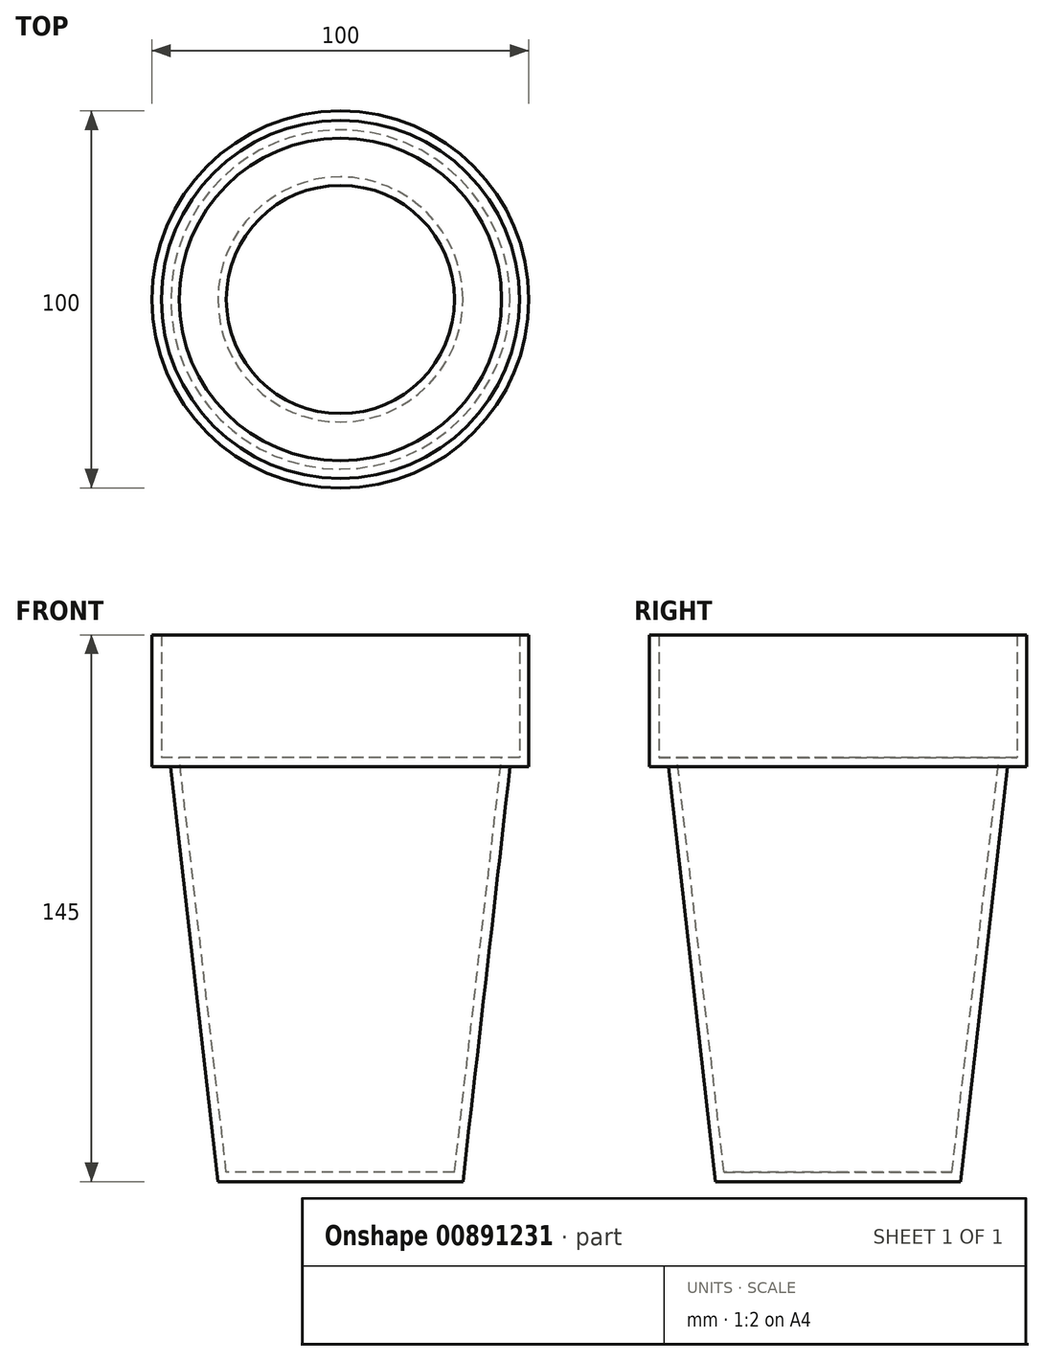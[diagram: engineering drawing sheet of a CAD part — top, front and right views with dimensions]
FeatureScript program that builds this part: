
annotation { "Feature Type Name" : "Feature", "Feature Type Description" : "" }
export const myFeature = defineFeature(function(context is Context, id is Id, definition is map)
    precondition{}
    {
        {
            var Q0;
            Q0=qCreatedBy(makeId("Top.planeOp"),FACE);
            var sketch = newSketch(context, id + "F0", { "sketchPlane" : qUnion([Q0])});
            skCircle(sketch, "E0", {"center": v(0, 0) * mm, "radius": 32.5 * mm});
            skSolve(sketch);
        }
        {
            var Q0;
            Q0=qCreatedBy(makeId("Top.planeOp"),FACE);
            cPlane(context, id + "F1", {"entities" : qUnion([Q0]), "cplaneType" : CPlaneType.OFFSET, "offset" : 110 * mm, "width" : 150 * mm, "height" : 150 * mm});
        }
        {
            var Q0;
            Q0=qCreatedBy(id+"F1.planeOp",FACE);
            var sketch = newSketch(context, id + "F2", { "sketchPlane" : qUnion([Q0])});
            skCircle(sketch, "E1", {"center": v(0, 0) * mm, "radius": 45 * mm});
            skSolve(sketch);
        }
        {
            var Q0;
            Q0=makeQuery(id+"F0.imprint","IMPRINT",FACE,{"disambiguationData":[TD([[makeQuery(id+"F0.imprint","IMPRINT",EDGE,{"derivedFrom":sQuery(id+"F0.wireOp",EDGE,"E0")}),1.0]])]});
            var Q1;
            Q1=makeQuery(id+"F2.imprint","IMPRINT",FACE,{"disambiguationData":[TD([[makeQuery(id+"F2.imprint","IMPRINT",EDGE,{"derivedFrom":sQuery(id+"F2.wireOp",EDGE,"E1")}),1.0]])]});
            loft(context, id + "F3", {"sheetProfilesArray" : [{ "sheetProfileEntities" : qUnion([Q0]) }, { "sheetProfileEntities" : qUnion([Q1]) }]});
        }
        {
            var Q0;
            Q0=makeQuery(id+"F3.opLoft","CAP_FACE",FACE,{"disambiguationData":[OSD([makeQuery(id+"F2.imprint","IMPRINT",FACE,{"disambiguationData":[TD([[makeQuery(id+"F2.imprint","IMPRINT",EDGE,{"derivedFrom":sQuery(id+"F2.wireOp",EDGE,"E1")}),1.0]])]})])],"isStart":true});
            var sketch = newSketch(context, id + "F4", { "sketchPlane" : qUnion([Q0])});
            skCircle(sketch, "E2", {"center": v(0, 0) * mm, "radius": 50 * mm});
            skSolve(sketch);
        }
        {
            var Q0;
            Q0 = qSketchRegion(id + "F4", true);
            extrude(context, id + "F5", {"entities" : qUnion([Q0]), "operationType" : NewBodyOperationType.ADD, "depth" : 35 * mm, "offsetDistance" : 25 * mm});
        }
        {
            var Q0;
            Q0=makeQuery(id+"F3.opLoft","CAP_FACE",FACE,{"disambiguationData":[OSD([makeQuery(id+"F2.imprint","IMPRINT",FACE,{"disambiguationData":[TD([[makeQuery(id+"F2.imprint","IMPRINT",EDGE,{"derivedFrom":sQuery(id+"F2.wireOp",EDGE,"E1")}),1.0]])]})])],"isStart":true});
            var Q1;
            Q1=makeQuery(id+"F5.opExtrude","CAP_FACE",FACE,{"disambiguationData":[OSD([sQuery(id+"F4.wireOp",EDGE,"E2")])],"isStart":false});
            shell(context, id + "F6", {"entities" : qUnion([Q0, Q1]), "thickness" : 2.5 * mm});
        }
    });
